# Revit family: BIM_Model_Synconta_901_B
name_source: partatom
category: Mechanical Equipment
revit_build: Autodesk Revit 2018 (Build: 20170223_1515(x64)
units: mm (PartAtom-declared; Revit-internal decimal feet)

## family parameters
Always vertical = Yes
Cut with Voids When Loaded = No
Part Type = Normal
Room Calculation Point = No
Round Connector Dimension = Use Radius
Shared = No
Work Plane-Based = No

## types (1)
- SYNCONTA 901B
    Cable or Vent Duct  DN 100 = 50 mm  [stored 0.164042 ft]
    Capacity = 977 litres
    Description = Synthetic prefabricated sump, designed as a single or doublepumping station for the automatic pumping of wastewater andsewage from locations and areas below the backwash level inaccordance with EN 12050-1.
    Inflow DN 150 = 75 mm
    Inflow DN 200 = 100 mm  [stored 0.328084 ft]
    Manufacturer = Sulzer
    Model = Synconta 901B
    Product Specification Link = https://www.sulzer.com 
https://www.sulzer.com
    Pump Discharge External Thread = 1 1/4"
    Tank Material = Polyethylene
    Weight (Kg) = 82kg (Without Pump)

note: [stored X ft] marks values corroborated as IEEE doubles in the binary element streams (Revit-internal decimal feet)

## geometry (parser evidence)
native form markers: Sweep x3
no freeform markers — native parametric forms only
